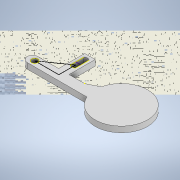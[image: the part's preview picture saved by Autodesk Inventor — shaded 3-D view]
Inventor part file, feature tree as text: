
AUTODESK INVENTOR PART (.ipt)
format: ipt  version: 2022 (Build 260153000, 153)  size: 179,712 bytes
history: native  units: mm
features: extrude x7, sketch x5, other x1
ambient origin geometry x8: Origin, YZ Plane, XZ Plane, XY Plane, X Axis, Y Axis, Z Axis, Center Point
bodies: Body1 (feature_tree)
feature tree (13):
  other  "Sólido1"
  sketch  "Boceto1"  dims[d0=100.0mm d1=20.0mm]
  extrude  "Extrusión1"  Depth=20.0mm
  extrude  "Extrusión2"  Depth=5.5mm TaperAngle=0.0deg
  sketch  "Boceto2"  dims[d2=30.0mm d3=5.5mm d4=0.0mm]
  extrude  "Extrusión3"  Depth=5.0mm
  extrude  "Extrusión4"  Depth=25.0mm
  extrude  "Extrusión5"  Depth=5.5mm
  extrude  "Extrusión6"  Depth=5.0mm
  extrude  "Extrusión7"  Depth=5.5mm
  sketch  "Boceto5"  dims[d10=10.0mm d11=20.0mm d12=5.0mm d13=15.0mm d14=1.0mm d15=5.5mm d16=0.0mm d17=5.5mm d18=0.0mm d19=5.5mm d20=0.0mm d21=2.0mm d22=6.0mm d23=5.5mm d24=0.0mm d25=15.0mm d26=0.0mm d27=50.0mm d28=5.5mm d29=0.0mm]
  sketch  "Boceto3"  dims[d5=5.5mm d6=0.0mm d7=5.0mm]
  sketch  "Boceto4"  dims[d8=25.0mm d9=30.0mm]
